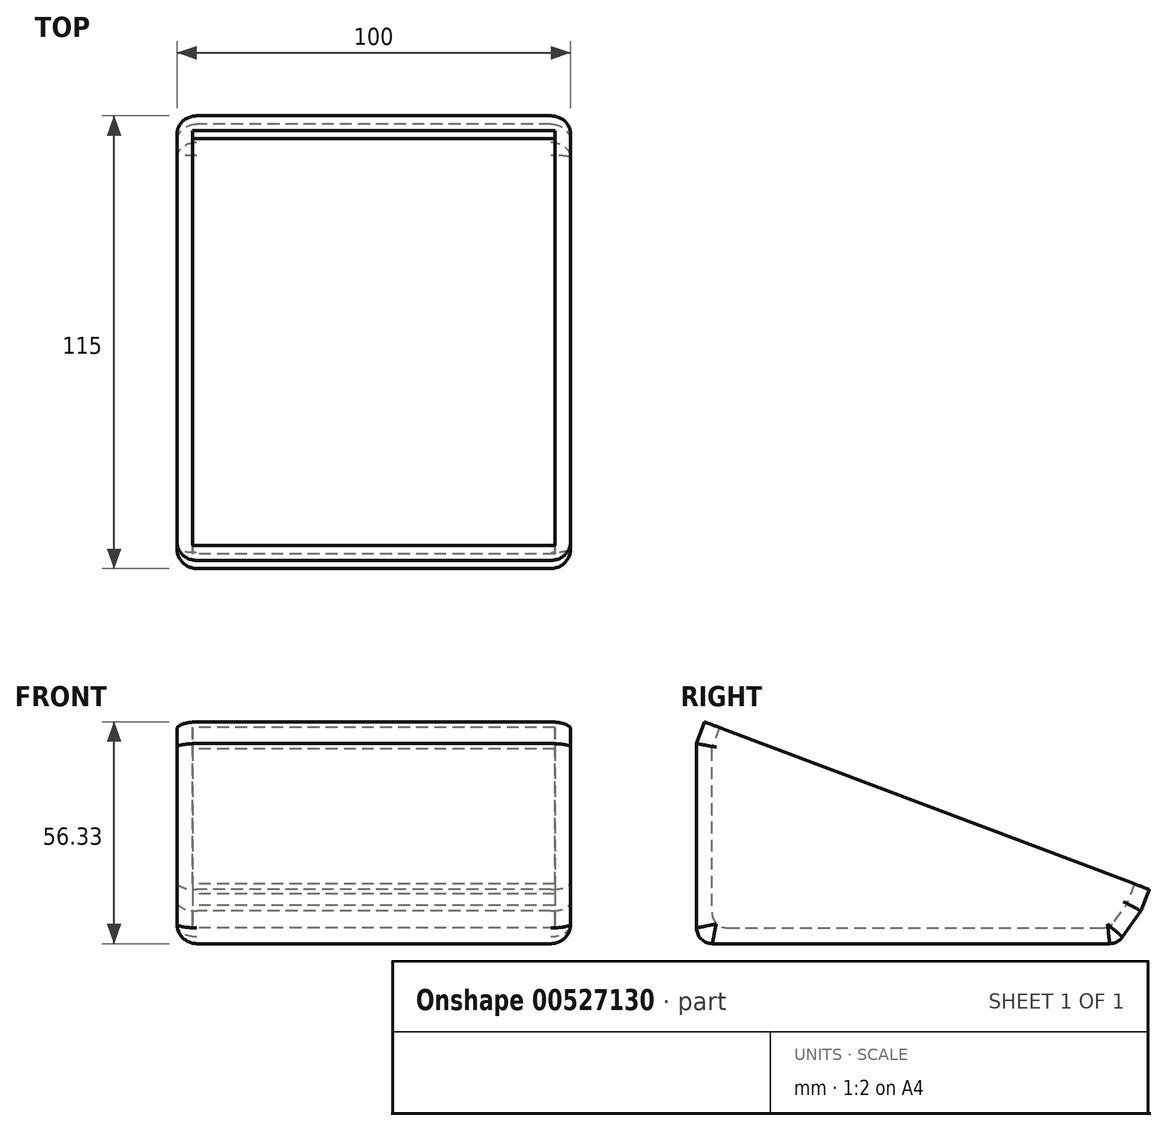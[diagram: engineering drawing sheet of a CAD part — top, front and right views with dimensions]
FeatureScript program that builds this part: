
annotation { "Feature Type Name" : "Feature", "Feature Type Description" : "" }
export const myFeature = defineFeature(function(context is Context, id is Id, definition is map)
    precondition{}
    {
        {
            var Q0;
            Q0=qCreatedBy(makeId("Right.planeOp"),FACE);
            var sketch = newSketch(context, id + "F0", { "sketchPlane" : qUnion([Q0])});
            skLineSegment(sketch, "E0", {"start": v(54.18, 1.67) * mm, "end": v(58.92, 8.28) * mm});
            skLineSegment(sketch, "E1", {"start": v(58.92, 8.28) * mm, "end": v(-54.01, 50.84) * mm});
            skLineSegment(sketch, "E2", {"start": v(-54.01, 50.84) * mm, "end": v(-54.01, 4) * mm});
            skLineSegment(sketch, "E3", {"start": v(-50.01, 0) * mm, "end": v(50.93, 0) * mm});
            skLineSegment(sketch, "E4", {"start": v(58.92, 8.28) * mm, "end": v(61, 13.78) * mm});
            skLineSegment(sketch, "E5", {"start": v(61, 13.78) * mm, "end": v(-51.94, 56.33) * mm});
            skLineSegment(sketch, "E6", {"start": v(-54.01, 50.84) * mm, "end": v(-51.94, 56.33) * mm});
            skPoint(sketch, "E7.visualSharp", {"position": v(52.99, 0) * mm});
            skArc(sketch, "E7.filletArc", {"start": v(50.93, 0) * mm, "mid": v(52.76, 0.44) * mm, "end": v(54.18, 1.67) * mm});
            skPoint(sketch, "E8.visualSharp", {"position": v(-54.01, 0) * mm});
            skArc(sketch, "E8.filletArc", {"start": v(-54.01, 4) * mm, "mid": v(-52.84, 1.17) * mm, "end": v(-50.01, 0) * mm});
            skLineSegment(sketch, "E9", {"start": v(61, 13.78) * mm, "end": v(57.25, 15.19) * mm});
            skLineSegment(sketch, "E10", {"start": v(57.25, 15.19) * mm, "end": v(55.18, 9.7) * mm});
            skLineSegment(sketch, "E11", {"start": v(-51.94, 56.33) * mm, "end": v(-48.2, 54.92) * mm});
            skLineSegment(sketch, "E12", {"start": v(-48.2, 54.92) * mm, "end": v(-50.27, 49.43) * mm});
            skLineSegment(sketch, "E13", {"start": v(-50.27, 49.43) * mm, "end": v(-50.27, 12.6) * mm});
            skLineSegment(sketch, "E14", {"start": v(-50.27, 12.6) * mm, "end": v(-50.13, 7.88) * mm});
            skLineSegment(sketch, "E15", {"start": v(-46.13, 4) * mm, "end": v(48.92, 4) * mm});
            skLineSegment(sketch, "E16", {"start": v(52.13, 5.6) * mm, "end": v(55.18, 9.7) * mm});
            skArc(sketch, "E17.filletArc", {"start": v(-50.13, 7.88) * mm, "mid": v(-48.92, 5.13) * mm, "end": v(-46.13, 4) * mm});
            skArc(sketch, "E18.filletArc", {"start": v(48.92, 4) * mm, "mid": v(50.72, 4.42) * mm, "end": v(52.13, 5.6) * mm});
            skSolve(sketch);
        }
        {
            var Q0;
            {var subQ0=sQuery(id+"F0.wireOp",EDGE,"E6");Q0=makeQuery(id+"F0.imprint","IMPRINT",FACE,{"disambiguationData":[TD([[makeQuery(id+"F0.imprint","IMPRINT",EDGE,{"derivedFrom":subQ0}),-1.0]])]});}
            var Q1;
            {var subQ0=sQuery(id+"F0.wireOp",EDGE,"E0");Q1=makeQuery(id+"F0.imprint","IMPRINT",FACE,{"disambiguationData":[TD([[makeQuery(id+"F0.imprint","IMPRINT",EDGE,{"derivedFrom":subQ0}),1.0]])]});}
            var Q2;
            {var subQ0=sQuery(id+"F0.wireOp",EDGE,"E4");Q2=makeQuery(id+"F0.imprint","IMPRINT",FACE,{"disambiguationData":[TD([[makeQuery(id+"F0.imprint","IMPRINT",EDGE,{"derivedFrom":subQ0}),1.0]])]});}
            extrude(context, id + "F1", {"entities" : qUnion([Q0, Q1, Q2]), "depth" : 46 * mm, "offsetDistance" : 25 * mm, "hasSecondDirection" : true, "secondDirectionOppositeDirection" : true, "secondDirectionDepth" : 46 * mm});
        }
        {
            var Q0;
            Q0=makeQuery(id+"F1.opExtrude","CAP_FACE",FACE,{"disambiguationData":[OSD([sQuery(id+"F0.wireOp",EDGE,"E0"),sQuery(id+"F0.wireOp",EDGE,"E2"),sQuery(id+"F0.wireOp",EDGE,"E3"),sQuery(id+"F0.wireOp",EDGE,"E4"),sQuery(id+"F0.wireOp",EDGE,"E6"),sQuery(id+"F0.wireOp",EDGE,"E7.filletArc"),sQuery(id+"F0.wireOp",EDGE,"E8.filletArc"),sQuery(id+"F0.wireOp",EDGE,"E9"),sQuery(id+"F0.wireOp",EDGE,"E10"),sQuery(id+"F0.wireOp",EDGE,"E11"),sQuery(id+"F0.wireOp",EDGE,"E12"),sQuery(id+"F0.wireOp",EDGE,"E13"),sQuery(id+"F0.wireOp",EDGE,"E14"),sQuery(id+"F0.wireOp",EDGE,"E15"),sQuery(id+"F0.wireOp",EDGE,"E16"),sQuery(id+"F0.wireOp",EDGE,"E17.filletArc"),sQuery(id+"F0.wireOp",EDGE,"E18.filletArc")])],"isStart":false});
            var sketch = newSketch(context, id + "F2", { "sketchPlane" : qUnion([Q0])});
            skLineSegment(sketch, "E19", {"start": v(54.18, 1.67) * mm, "end": v(58.92, 8.28) * mm});
            skLineSegment(sketch, "E20", {"start": v(58.92, 8.28) * mm, "end": v(-54.01, 50.84) * mm});
            skLineSegment(sketch, "E21", {"start": v(-54.01, 50.84) * mm, "end": v(-54.01, 4) * mm});
            skLineSegment(sketch, "E22", {"start": v(-50.01, 0) * mm, "end": v(50.93, 0) * mm});
            skLineSegment(sketch, "E23", {"start": v(58.92, 8.28) * mm, "end": v(61, 13.78) * mm});
            skLineSegment(sketch, "E24", {"start": v(61, 13.78) * mm, "end": v(-51.94, 56.33) * mm});
            skLineSegment(sketch, "E25", {"start": v(-54.01, 50.84) * mm, "end": v(-51.94, 56.33) * mm});
            skPoint(sketch, "E26.visualSharp", {"position": v(52.99, 0) * mm});
            skArc(sketch, "E26.filletArc", {"start": v(50.93, 0) * mm, "mid": v(52.76, 0.44) * mm, "end": v(54.18, 1.67) * mm});
            skPoint(sketch, "E27.visualSharp", {"position": v(-54.01, 0) * mm});
            skArc(sketch, "E27.filletArc", {"start": v(-54.01, 4) * mm, "mid": v(-52.84, 1.17) * mm, "end": v(-50.01, 0) * mm});
            skLineSegment(sketch, "E28", {"start": v(61, 13.78) * mm, "end": v(57.25, 15.19) * mm});
            skLineSegment(sketch, "E29", {"start": v(57.25, 15.19) * mm, "end": v(55.18, 9.7) * mm});
            skLineSegment(sketch, "E30", {"start": v(-51.94, 56.33) * mm, "end": v(-48.2, 54.92) * mm});
            skLineSegment(sketch, "E31", {"start": v(-48.2, 54.92) * mm, "end": v(-50.27, 49.43) * mm});
            skLineSegment(sketch, "E32", {"start": v(-50.27, 49.43) * mm, "end": v(-50.27, 12.6) * mm});
            skLineSegment(sketch, "E33", {"start": v(-50.27, 12.6) * mm, "end": v(-50.13, 7.88) * mm});
            skLineSegment(sketch, "E34", {"start": v(-46.13, 4) * mm, "end": v(48.92, 4) * mm});
            skLineSegment(sketch, "E35", {"start": v(52.13, 5.6) * mm, "end": v(55.18, 9.7) * mm});
            skArc(sketch, "E36.filletArc", {"start": v(-50.13, 7.88) * mm, "mid": v(-48.92, 5.13) * mm, "end": v(-46.13, 4) * mm});
            skArc(sketch, "E37.filletArc", {"start": v(48.92, 4) * mm, "mid": v(50.72, 4.42) * mm, "end": v(52.13, 5.6) * mm});
            skSolve(sketch);
        }
        {
            var Q0;
            Q0=makeQuery(id+"F2.imprint","IMPRINT",FACE,{"disambiguationData":[TD([[makeQuery(id+"F2.imprint","IMPRINT",EDGE,{"derivedFrom":sQuery(id+"F2.wireOp",EDGE,"E24")}),1.0]])]});
            var Q1;
            {var subQ0=sQuery(id+"F2.wireOp",EDGE,"E23");Q1=makeQuery(id+"F2.imprint","IMPRINT",FACE,{"disambiguationData":[TD([[makeQuery(id+"F2.imprint","IMPRINT",EDGE,{"derivedFrom":subQ0}),1.0]])]});}
            var Q2;
            {var subQ0=sQuery(id+"F2.wireOp",EDGE,"E19");Q2=makeQuery(id+"F2.imprint","IMPRINT",FACE,{"disambiguationData":[TD([[makeQuery(id+"F2.imprint","IMPRINT",EDGE,{"derivedFrom":subQ0}),1.0]])]});}
            var Q3;
            {var subQ0=sQuery(id+"F2.wireOp",EDGE,"E25");Q3=makeQuery(id+"F2.imprint","IMPRINT",FACE,{"disambiguationData":[TD([[makeQuery(id+"F2.imprint","IMPRINT",EDGE,{"derivedFrom":subQ0}),-1.0]])]});}
            var Q4;
            {var subQ0=sQuery(id+"F2.wireOp",EDGE,"E32");Q4=makeQuery(id+"F2.imprint","IMPRINT",FACE,{"disambiguationData":[TD([[makeQuery(id+"F2.imprint","IMPRINT",EDGE,{"derivedFrom":subQ0}),1.0]])]});}
            extrude(context, id + "F3", {"entities" : qUnion([Q0, Q1, Q2, Q3, Q4]), "operationType" : NewBodyOperationType.ADD, "depth" : 4 * mm, "offsetDistance" : 25 * mm});
        }
        {
            var Q0;
            Q0=makeQuery(id+"F1.opExtrude","CAP_FACE",FACE,{"disambiguationData":[OSD([sQuery(id+"F0.wireOp",EDGE,"E0"),sQuery(id+"F0.wireOp",EDGE,"E2"),sQuery(id+"F0.wireOp",EDGE,"E3"),sQuery(id+"F0.wireOp",EDGE,"E4"),sQuery(id+"F0.wireOp",EDGE,"E6"),sQuery(id+"F0.wireOp",EDGE,"E7.filletArc"),sQuery(id+"F0.wireOp",EDGE,"E8.filletArc"),sQuery(id+"F0.wireOp",EDGE,"E9"),sQuery(id+"F0.wireOp",EDGE,"E10"),sQuery(id+"F0.wireOp",EDGE,"E11"),sQuery(id+"F0.wireOp",EDGE,"E12"),sQuery(id+"F0.wireOp",EDGE,"E13"),sQuery(id+"F0.wireOp",EDGE,"E14"),sQuery(id+"F0.wireOp",EDGE,"E15"),sQuery(id+"F0.wireOp",EDGE,"E16"),sQuery(id+"F0.wireOp",EDGE,"E17.filletArc"),sQuery(id+"F0.wireOp",EDGE,"E18.filletArc")])],"isStart":true});
            var sketch = newSketch(context, id + "F4", { "sketchPlane" : qUnion([Q0])});
            skLineSegment(sketch, "E38", {"start": v(-61, 13.78) * mm, "end": v(51.94, 56.33) * mm});
            skLineSegment(sketch, "E39", {"start": v(51.94, 56.33) * mm, "end": v(54.01, 50.84) * mm});
            skLineSegment(sketch, "E40", {"start": v(54.01, 50.84) * mm, "end": v(54.01, 4) * mm});
            skLineSegment(sketch, "E41", {"start": v(50.01, 0) * mm, "end": v(-50.93, 0) * mm});
            skLineSegment(sketch, "E42", {"start": v(-61, 13.78) * mm, "end": v(-58.92, 8.28) * mm});
            skLineSegment(sketch, "E43", {"start": v(-58.92, 8.28) * mm, "end": v(-54.18, 1.67) * mm});
            skPoint(sketch, "E44.visualSharp", {"position": v(54.01, 0) * mm});
            skArc(sketch, "E44.filletArc", {"start": v(50.01, 0) * mm, "mid": v(52.84, 1.17) * mm, "end": v(54.01, 4) * mm});
            skPoint(sketch, "E45.visualSharp", {"position": v(-52.99, 0) * mm});
            skArc(sketch, "E45.filletArc", {"start": v(-54.18, 1.67) * mm, "mid": v(-52.76, 0.44) * mm, "end": v(-50.93, 0) * mm});
            skSolve(sketch);
        }
        {
            var Q0;
            {var subQ4=sQuery(id+"F4.wireOp",EDGE,"E39");Q0=makeQuery(id+"F4.imprint","IMPRINT",FACE,{"disambiguationData":[TD([[makeQuery(id+"F4.imprint","IMPRINT",EDGE,{"derivedFrom":subQ4}),1.0]])]});}
            var Q1;
            {var subQ2=makeQuery(id+"F1.opExtrude","CAP_EDGE",EDGE,{"disambiguationData":[OSD([sQuery(id+"F0.wireOp",EDGE,"E10")])],"isStart":true});Q1=makeQuery(id+"F4.imprint","IMPRINT",FACE,{"disambiguationData":[TD([[makeQuery(id+"F4.imprint","IMPRINT",EDGE,{"derivedFrom":subQ2}),1.0]])]});}
            extrude(context, id + "F5", {"entities" : qUnion([Q0, Q1]), "operationType" : NewBodyOperationType.ADD, "depth" : 4 * mm, "offsetDistance" : 25 * mm});
        }
        {
            var Q0;
            Q0=makeQuery(id+"F3.opExtrude","CAP_EDGE",EDGE,{"disambiguationData":[OSD([sQuery(id+"F2.wireOp",EDGE,"E25")])],"isStart":false});
            var Q1;
            Q1=makeQuery(id+"F5.opExtrude","CAP_EDGE",EDGE,{"disambiguationData":[OSD([sQuery(id+"F4.wireOp",EDGE,"E39")])],"isStart":false});
            var Q2;
            Q2=makeQuery(id+"F5.opExtrude","CAP_EDGE",EDGE,{"disambiguationData":[OSD([sQuery(id+"F4.wireOp",EDGE,"E42")])],"isStart":false});
            var Q3;
            Q3=makeQuery(id+"F3.opExtrude","CAP_EDGE",EDGE,{"disambiguationData":[OSD([sQuery(id+"F2.wireOp",EDGE,"E23")])],"isStart":false});
            var Q4;
            Q4=makeQuery(id+"F3.opExtrude","CAP_EDGE",EDGE,{"disambiguationData":[OSD([sQuery(id+"F2.wireOp",EDGE,"E22")])],"isStart":false});
            var Q5;
            Q5=makeQuery(id+"F5.opExtrude","CAP_EDGE",EDGE,{"disambiguationData":[OSD([sQuery(id+"F4.wireOp",EDGE,"E41")])],"isStart":false});
            fillet(context, id + "F6", {"entities" : qUnion([Q0, Q1, Q2, Q3, Q4, Q5]), "radius" : 5 * mm, "tangentPropagation" : true, "allowEdgeOverflow" : false});
        }
    });
